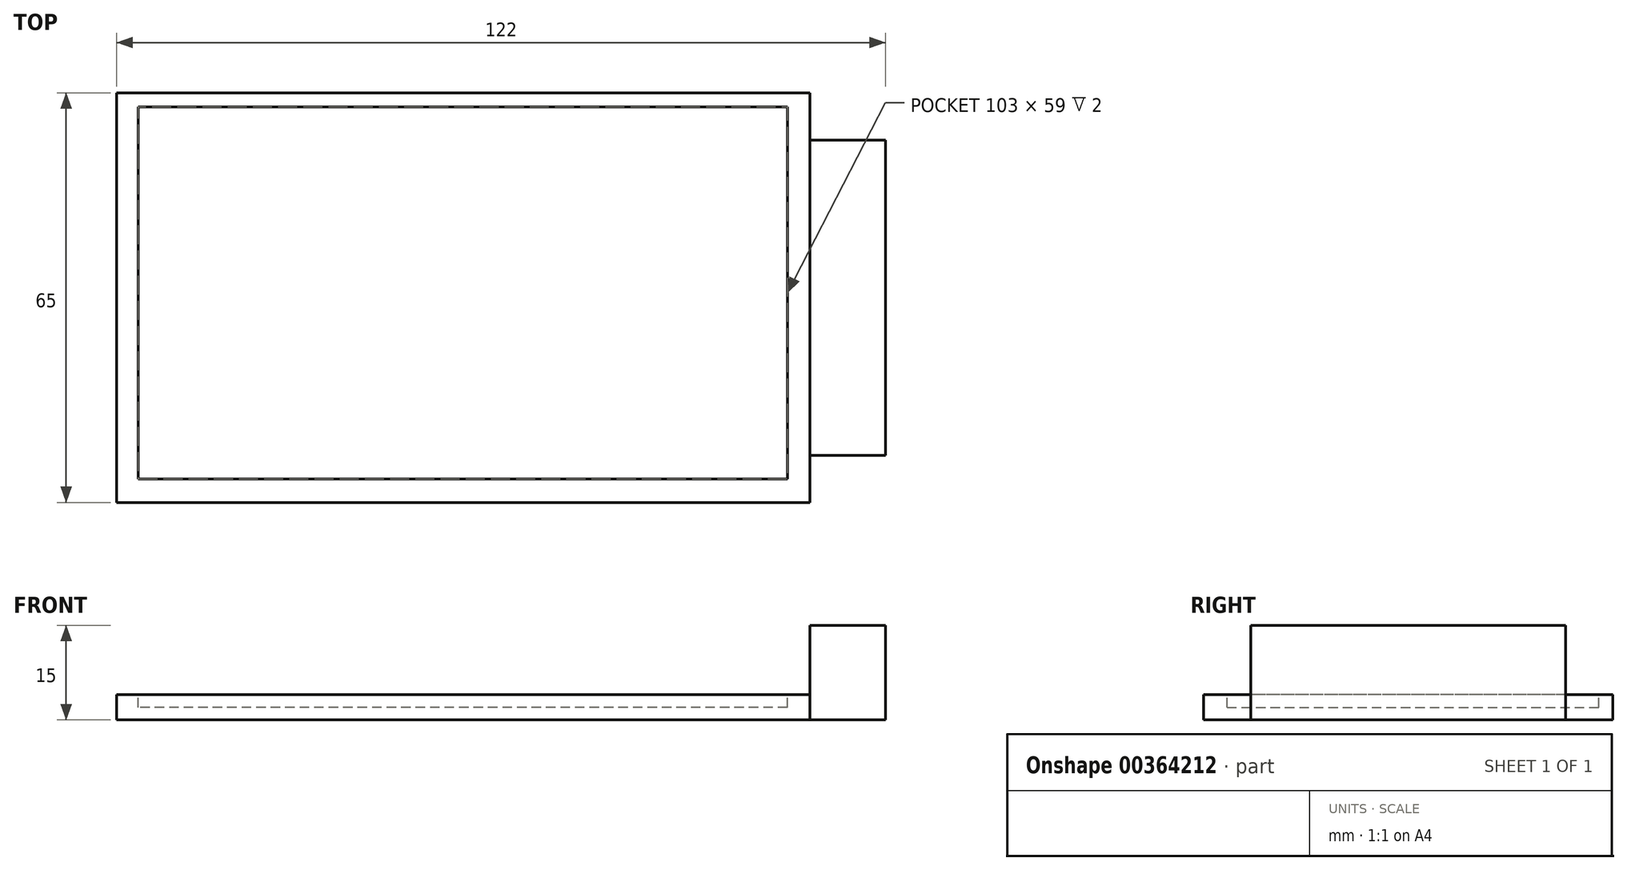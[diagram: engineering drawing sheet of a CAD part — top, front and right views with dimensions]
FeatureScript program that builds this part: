
annotation { "Feature Type Name" : "Feature", "Feature Type Description" : "" }
export const myFeature = defineFeature(function(context is Context, id is Id, definition is map)
    precondition{}
    {
        {
            var Q0;
            Q0=qCreatedBy(makeId("Top.planeOp"),FACE);
            var sketch = newSketch(context, id + "F0", { "sketchPlane" : qUnion([Q0])});
            skLineSegment(sketch, "E0.bottom", {"start": v(-57.48, 17.01) * mm, "end": v(52.52, 17.01) * mm});
            skLineSegment(sketch, "E0.top", {"start": v(-57.48, -47.99) * mm, "end": v(52.52, -47.99) * mm});
            skLineSegment(sketch, "E0.left", {"start": v(-57.48, 17.01) * mm, "end": v(-57.48, -47.99) * mm});
            skLineSegment(sketch, "E1.bottom", {"start": v(10.94, 17.01) * mm, "end": v(-39.06, 17.01) * mm});
            skLineSegment(sketch, "E2.bottom", {"start": v(52.52, -40.49) * mm, "end": v(64.52, -40.49) * mm});
            skLineSegment(sketch, "E2.top", {"start": v(52.52, 9.51) * mm, "end": v(64.52, 9.51) * mm});
            skLineSegment(sketch, "E2.right", {"start": v(64.52, -40.49) * mm, "end": v(64.52, 9.51) * mm});
            skLineSegment(sketch, "E3", {"start": v(52.52, -47.99) * mm, "end": v(52.52, -40.49) * mm});
            skLineSegment(sketch, "E4", {"start": v(52.52, 9.51) * mm, "end": v(52.52, 17.01) * mm});
            skLineSegment(sketch, "E5", {"start": v(52.52, -40.49) * mm, "end": v(52.52, 9.51) * mm});
            skSolve(sketch);
        }
        {
            var Q0;
            Q0 = qSketchRegion(id + "F0", true);
            extrude(context, id + "F1", {"entities" : qUnion([Q0]), "depth" : 4 * mm});
        }
        {
            var Q0;
            Q0=makeQuery(id+"F1.opExtrude","CAP_FACE",FACE,{"disambiguationData":[OSD([sQuery(id+"F0.wireOp",EDGE,"E0.bottom"),sQuery(id+"F0.wireOp",EDGE,"E0.top"),sQuery(id+"F0.wireOp",EDGE,"E0.left"),sQuery(id+"F0.wireOp",EDGE,"E1.bottom"),sQuery(id+"F0.wireOp",EDGE,"E2.bottom"),sQuery(id+"F0.wireOp",EDGE,"E2.top"),sQuery(id+"F0.wireOp",EDGE,"E2.right"),sQuery(id+"F0.wireOp",EDGE,"E3"),sQuery(id+"F0.wireOp",EDGE,"E4")])],"isStart":false});
            var sketch = newSketch(context, id + "F2", { "sketchPlane" : qUnion([Q0])});
            skPoint(sketch, "E6.oppositeSnap0", {"position": v(52.52, -44.24) * mm});
            skLineSegment(sketch, "E6.bottom", {"start": v(-54.04, 14.76) * mm, "end": v(48.96, 14.76) * mm});
            skLineSegment(sketch, "E6.top", {"start": v(-54.04, -44.24) * mm, "end": v(48.96, -44.24) * mm});
            skLineSegment(sketch, "E6.left", {"start": v(-54.04, 14.76) * mm, "end": v(-54.04, -44.24) * mm});
            skLineSegment(sketch, "E6.right", {"start": v(48.96, 14.76) * mm, "end": v(48.96, -44.24) * mm});
            skSolve(sketch);
        }
        {
            var Q0;
            Q0=makeQuery(id+"F2.imprint","IMPRINT",FACE,{"disambiguationData":[TD([[makeQuery(id+"F2.imprint","IMPRINT",EDGE,{"derivedFrom":sQuery(id+"F2.wireOp",EDGE,"E6.bottom")}),-1.0]])]});
            extrude(context, id + "F3", {"entities" : qUnion([Q0]), "operationType" : NewBodyOperationType.REMOVE, "oppositeDirection" : true, "depth" : 8 * mm});
        }
        {
            var Q0;
            Q0=makeQuery(id+"F0.imprint","IMPRINT",FACE,{"disambiguationData":[TD([[makeQuery(id+"F0.imprint","IMPRINT",EDGE,{"derivedFrom":sQuery(id+"F0.wireOp",EDGE,"E2.bottom")}),1.0]])]});
            extrude(context, id + "F4", {"entities" : qUnion([Q0]), "operationType" : NewBodyOperationType.ADD, "depth" : 15 * mm});
        }
        {
            var Q0;
            Q0=makeQuery(id+"F0.imprint","IMPRINT",FACE,{"disambiguationData":[TD([[makeQuery(id+"F0.imprint","IMPRINT",EDGE,{"derivedFrom":sQuery(id+"F0.wireOp",EDGE,"E0.top")}),1.0]])]});
            extrude(context, id + "F5", {"entities" : qUnion([Q0]), "operationType" : NewBodyOperationType.ADD, "depth" : 2 * mm});
        }
    });
